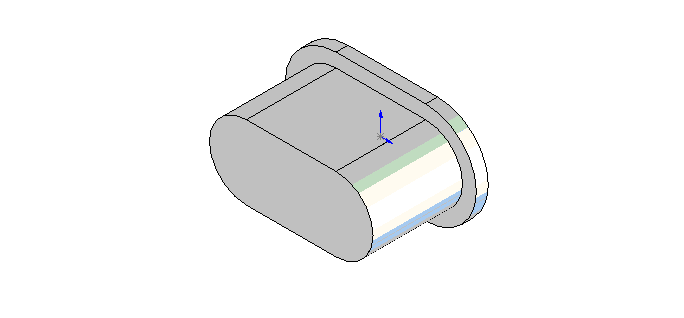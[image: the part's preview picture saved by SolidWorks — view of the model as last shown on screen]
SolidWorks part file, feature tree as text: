
SOLIDWORKS PART (.sldprt)
format: sldprt  version: not decoded by parser v0  size: 84,480 bytes
history: native  units: mm
features: sketch x4, plane x3, extrude x2, hole x1 + 1 further entry (+7 scaffold rows collapsed)
feature tree (18):
  scaffold x7  (default folders/planes/origin — collapsed)
  "Corps de surface"
  plane  "Face"
  plane  "Dessus"
  plane  "Droite"
  sketch  "Esquisse1"  dims[D1=17.0mm D2=15.0mm]
  extrude  "Extrusion1"  Depth=2mm
  sketch  "Esquisse3"  dims[D1=12.4mm D2=15.0mm]
  extrude  "Extrusion2"  Depth=15mm
  hole  "Dégagement pour M41"  Diameter=4.5mm Depth=17mm
  sketch  "Esquisse5"
  sketch  "Esquisse4"  dims[hole-wizard template sketch: 60 standard entries collapsed; hole parameters kept: c18.Profondeur du perçage jusqu'au prochain=17.0mm]
decode coverage: 6 of 7 modeling features carry decoded parameters; 1 rows unclassified (native names shown)
note: ~ marks probable driven/reference dimensions
note: suppression state not decoded; provenance and decode notes live in map.json
